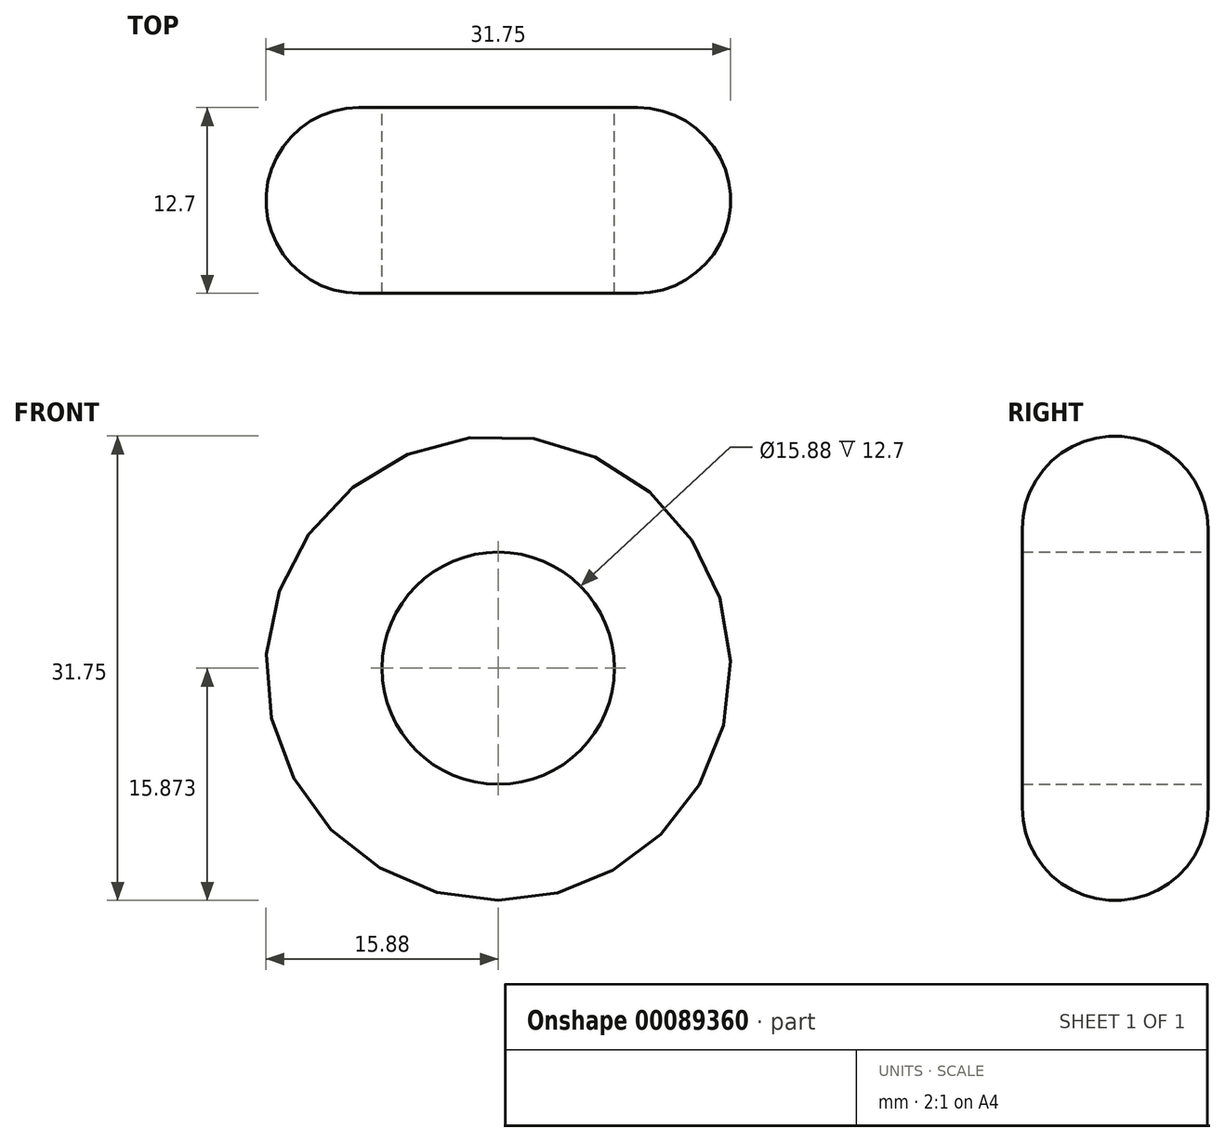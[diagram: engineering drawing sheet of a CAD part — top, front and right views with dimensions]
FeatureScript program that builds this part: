
annotation { "Feature Type Name" : "Feature", "Feature Type Description" : "" }
export const myFeature = defineFeature(function(context is Context, id is Id, definition is map)
    precondition{}
    {
        {
            var Q0;
            Q0=qCreatedBy(makeId("Front.planeOp"),FACE);
            var sketch = newSketch(context, id + "F0", { "sketchPlane" : qUnion([Q0])});
            skCircle(sketch, "E0", {"center": v(-29.44, 24.13) * mm, "radius": 15.88 * mm});
            skCircle(sketch, "E1", {"center": v(-29.44, 24.13) * mm, "radius": 7.94 * mm});
            skSolve(sketch);
        }
        {
            var Q0;
            Q0=qSketchRegion(id+"F0",true);
            extrude(context, id + "F1", {"entities" : qUnion([Q0]), "depth" : 12.7 * mm});
        }
        {
            var Q0;
            Q0=makeQuery(id+"F1.opExtrude","CAP_EDGE",EDGE,{"disambiguationData":[OSD([sQuery(id+"F0.wireOp",EDGE,"E0")])],"isStart":false});
            var Q1;
            Q1=makeQuery(id+"F1.opExtrude","CAP_EDGE",EDGE,{"disambiguationData":[OSD([sQuery(id+"F0.wireOp",EDGE,"E0")])],"isStart":true});
            fillet(context, id + "F2", {"entities" : qUnion([Q0, Q1]), "radius" : 6.35 * mm, "tangentPropagation" : true, "allowEdgeOverflow" : false});
        }
    });
